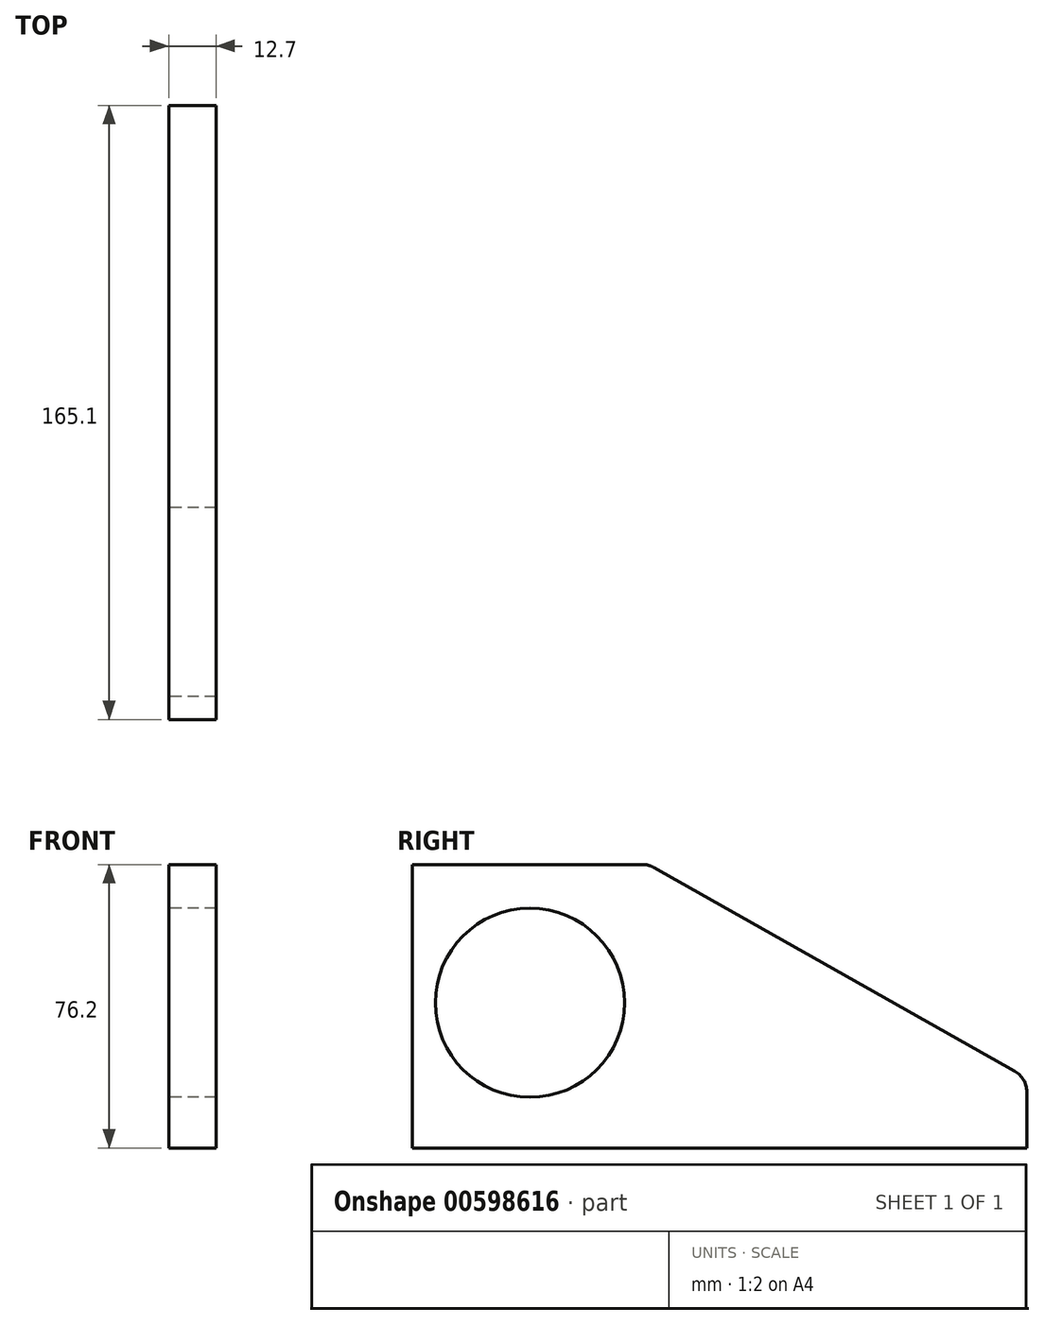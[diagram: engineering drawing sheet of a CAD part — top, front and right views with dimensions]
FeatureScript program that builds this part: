
annotation { "Feature Type Name" : "Feature", "Feature Type Description" : "" }
export const myFeature = defineFeature(function(context is Context, id is Id, definition is map)
    precondition{}
    {
        {
            var Q0;
            Q0=qCreatedBy(makeId("Right.planeOp"),FACE);
            var sketch = newSketch(context, id + "F0", { "sketchPlane" : qUnion([Q0])});
            skLineSegment(sketch, "E0.bottom", {"start": v(-37.18, 21.1) * mm, "end": v(24.65, 21.1) * mm});
            skLineSegment(sketch, "E0.top", {"start": v(-37.18, -55.1) * mm, "end": v(127.92, -55.1) * mm});
            skLineSegment(sketch, "E0.left", {"start": v(-37.18, 21.1) * mm, "end": v(-37.18, -55.1) * mm});
            skLineSegment(sketch, "E0.right", {"start": v(127.92, -40.01) * mm, "end": v(127.92, -55.1) * mm});
            skLineSegment(sketch, "E1", {"start": v(127.92, -55.1) * mm, "end": v(26.32, -55.1) * mm});
            skLineSegment(sketch, "E2", {"start": v(26.32, -55.1) * mm, "end": v(26.32, 21.1) * mm, "construction": true});
            skLineSegment(sketch, "E3", {"start": v(124.69, -34.49) * mm, "end": v(27.77, 20.28) * mm});
            skCircle(sketch, "E4", {"center": v(-5.58, -16.08) * mm, "radius": 25.4 * mm});
            skPoint(sketch, "E5.visualSharp", {"position": v(127.92, -36.3) * mm});
            skArc(sketch, "E5.filletArc", {"start": v(127.92, -40.01) * mm, "mid": v(127.05, -36.81) * mm, "end": v(124.69, -34.49) * mm});
            skArc(sketch, "E6.filletArc", {"start": v(27.77, 20.28) * mm, "mid": v(26.26, 20.9) * mm, "end": v(24.65, 21.1) * mm});
            skSolve(sketch);
        }
        {
            var Q0;
            Q0=makeQuery(id+"F0.imprint","IMPRINT",FACE,{"disambiguationData":[TD([[makeQuery(id+"F0.imprint","IMPRINT",EDGE,{"derivedFrom":sQuery(id+"F0.wireOp",EDGE,"E0.bottom")}),-1.0]])]});
            extrude(context, id + "F1", {"entities" : qUnion([Q0]), "depth" : 12.7 * mm, "offsetDistance" : 25.4 * mm});
        }
    });
